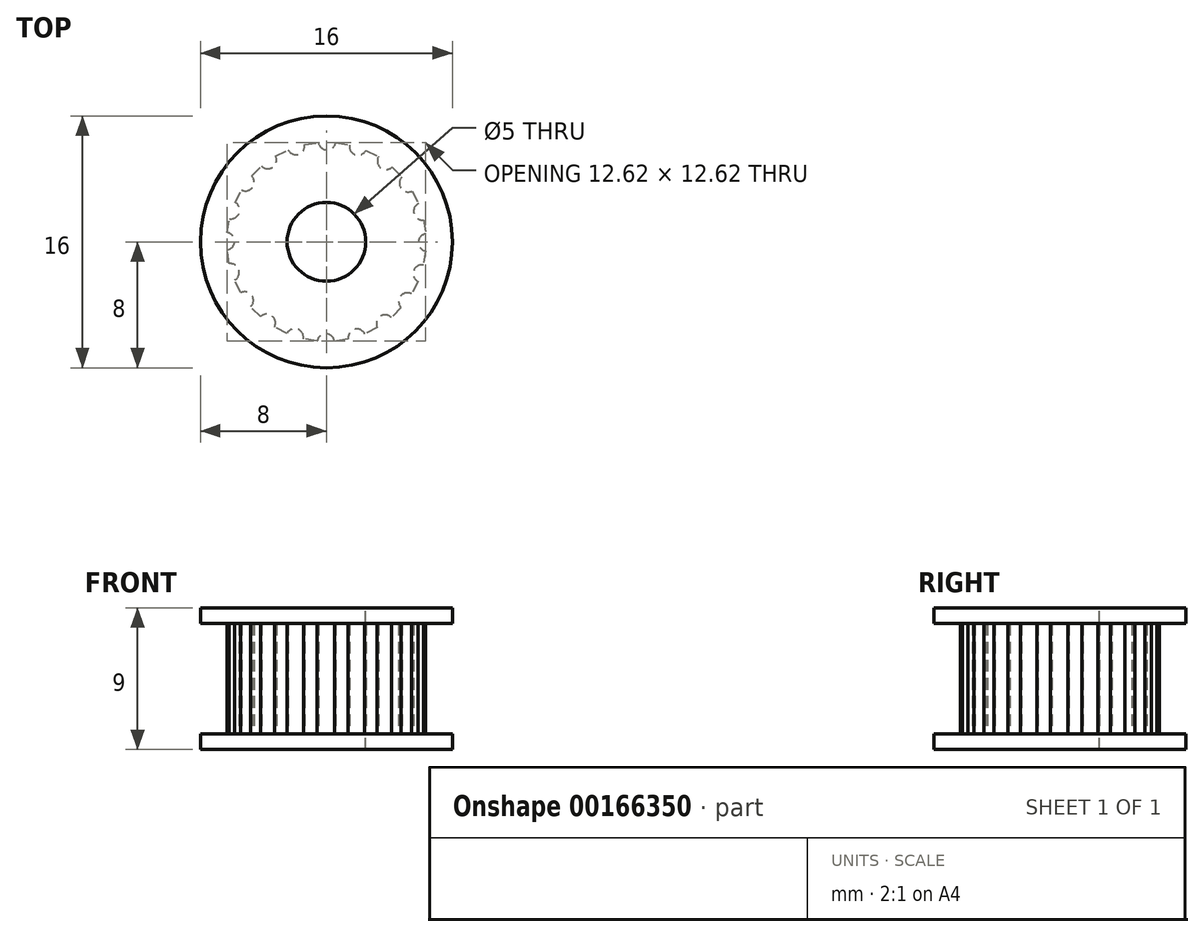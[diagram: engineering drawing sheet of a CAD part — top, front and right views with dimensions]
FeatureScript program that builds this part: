
annotation { "Feature Type Name" : "Feature", "Feature Type Description" : "" }
export const myFeature = defineFeature(function(context is Context, id is Id, definition is map)
    precondition{}
    {
        {
            var Q0;
            Q0=qCreatedBy(makeId("Top.planeOp"),FACE);
            var sketch = newSketch(context, id + "F0", { "sketchPlane" : qUnion([Q0])});
            skCircle(sketch, "E0", {"center": v(0, 0) * mm, "radius": 8 * mm});
            skSolve(sketch);
        }
        {
            var Q0;
            Q0 = qSketchRegion(id + "F0", true);
            extrude(context, id + "F1", {"entities" : qUnion([Q0]), "depth" : 1 * mm});
        }
        {
            var Q0;
            Q0=makeQuery(id+"F1.opExtrude","CAP_FACE",FACE,{"disambiguationData":[OSD([sQuery(id+"F0.wireOp",EDGE,"E0")])],"isStart":false});
            var sketch = newSketch(context, id + "F2", { "sketchPlane" : qUnion([Q0])});
            skCircle(sketch, "E1.cCircle", {"center": v(0, 0) * mm, "radius": 6.4 * mm, "construction": true});
            skLineSegment(sketch, "E1.0", {"start": v(2.01, 6.07) * mm, "end": v(3.79, 5.15) * mm});
            skLineSegment(sketch, "E1.1", {"start": v(3.79, 5.15) * mm, "end": v(5.2, 3.72) * mm});
            skLineSegment(sketch, "E1.2", {"start": v(5.2, 3.72) * mm, "end": v(6.1, 1.94) * mm});
            skLineSegment(sketch, "E1.3", {"start": v(6.1, 1.94) * mm, "end": v(6.4, -0.04) * mm});
            skLineSegment(sketch, "E1.4", {"start": v(6.4, -0.04) * mm, "end": v(6.07, -2.01) * mm});
            skLineSegment(sketch, "E1.5", {"start": v(6.07, -2.01) * mm, "end": v(5.15, -3.79) * mm});
            skLineSegment(sketch, "E1.6", {"start": v(5.15, -3.79) * mm, "end": v(3.72, -5.2) * mm});
            skLineSegment(sketch, "E1.7", {"start": v(3.72, -5.2) * mm, "end": v(1.94, -6.1) * mm});
            skLineSegment(sketch, "E1.8", {"start": v(1.94, -6.1) * mm, "end": v(-0.04, -6.4) * mm});
            skLineSegment(sketch, "E1.9", {"start": v(-0.04, -6.4) * mm, "end": v(-2.01, -6.07) * mm});
            skLineSegment(sketch, "E1.10", {"start": v(-2.01, -6.07) * mm, "end": v(-3.79, -5.15) * mm});
            skLineSegment(sketch, "E1.11", {"start": v(-3.79, -5.15) * mm, "end": v(-5.2, -3.72) * mm});
            skLineSegment(sketch, "E1.12", {"start": v(-5.2, -3.72) * mm, "end": v(-6.1, -1.94) * mm});
            skLineSegment(sketch, "E1.13", {"start": v(-6.1, -1.94) * mm, "end": v(-6.4, 0.04) * mm});
            skLineSegment(sketch, "E1.14", {"start": v(-6.4, 0.04) * mm, "end": v(-6.07, 2.01) * mm});
            skLineSegment(sketch, "E1.15", {"start": v(-6.07, 2.01) * mm, "end": v(-5.15, 3.79) * mm});
            skLineSegment(sketch, "E1.16", {"start": v(-5.15, 3.79) * mm, "end": v(-3.72, 5.2) * mm});
            skLineSegment(sketch, "E1.17", {"start": v(-3.72, 5.2) * mm, "end": v(-1.94, 6.1) * mm});
            skLineSegment(sketch, "E1.18", {"start": v(-1.94, 6.1) * mm, "end": v(0.04, 6.4) * mm});
            skLineSegment(sketch, "E1.19", {"start": v(0.04, 6.4) * mm, "end": v(2.01, 6.07) * mm});
            skCircle(sketch, "E2", {"center": v(3.72, -5.2) * mm, "radius": 0.56 * mm});
            skCircle(sketch, "E3.1.0", {"center": v(5.15, -3.79) * mm, "radius": 0.56 * mm});
            skCircle(sketch, "E3.2.0", {"center": v(6.07, -2.01) * mm, "radius": 0.56 * mm});
            skCircle(sketch, "E3.3.0", {"center": v(6.4, -0.04) * mm, "radius": 0.56 * mm});
            skCircle(sketch, "E3.4.0", {"center": v(6.1, 1.94) * mm, "radius": 0.56 * mm});
            skCircle(sketch, "E3.5.0", {"center": v(5.2, 3.72) * mm, "radius": 0.56 * mm});
            skCircle(sketch, "E3.6.0", {"center": v(3.79, 5.15) * mm, "radius": 0.56 * mm});
            skCircle(sketch, "E3.7.0", {"center": v(2.01, 6.07) * mm, "radius": 0.55 * mm});
            skCircle(sketch, "E3.8.0", {"center": v(0.04, 6.4) * mm, "radius": 0.56 * mm});
            skCircle(sketch, "E3.9.0", {"center": v(-1.94, 6.1) * mm, "radius": 0.56 * mm});
            skCircle(sketch, "E3.10.0", {"center": v(-3.72, 5.2) * mm, "radius": 0.56 * mm});
            skCircle(sketch, "E3.11.0", {"center": v(-5.15, 3.79) * mm, "radius": 0.56 * mm});
            skCircle(sketch, "E3.12.0", {"center": v(-6.07, 2.01) * mm, "radius": 0.56 * mm});
            skCircle(sketch, "E3.13.0", {"center": v(-6.4, 0.04) * mm, "radius": 0.56 * mm});
            skCircle(sketch, "E3.14.0", {"center": v(-6.1, -1.94) * mm, "radius": 0.56 * mm});
            skCircle(sketch, "E3.15.0", {"center": v(-5.2, -3.72) * mm, "radius": 0.56 * mm});
            skCircle(sketch, "E3.16.0", {"center": v(-3.79, -5.15) * mm, "radius": 0.56 * mm});
            skCircle(sketch, "E3.17.0", {"center": v(-2.01, -6.07) * mm, "radius": 0.56 * mm});
            skCircle(sketch, "E3.18.0", {"center": v(-0.04, -6.4) * mm, "radius": 0.56 * mm});
            skCircle(sketch, "E3.19.0", {"center": v(1.94, -6.1) * mm, "radius": 0.56 * mm});
            skSolve(sketch);
        }
        {
            var Q0;
            {var subQ67=sQuery(id+"F2.wireOp",EDGE,"E3.7.0");var subQ77=sQuery(id+"F2.wireOp",EDGE,"E1.0");var subQ78=makeQuery(id+"F2.imprint","INTERSECT",VERTEX,{"derivedFrom":[subQ77,subQ67]});Q0=makeQuery(id+"F2.imprint","IMPRINT",FACE,{"disambiguationData":[TD([[makeQuery(id+"F2.imprint","IMPRINT",EDGE,{"disambiguationData":[TD([[subQ78,-1.0]])],"derivedFrom":subQ77}),-1.0]])]});}
            extrude(context, id + "F3", {"entities" : qUnion([Q0]), "operationType" : NewBodyOperationType.ADD, "depth" : 7 * mm});
        }
        {
            var Q0;
            Q0=makeQuery(id+"F3.opExtrude","CAP_FACE",FACE,{"disambiguationData":[OSD([sQuery(id+"F2.wireOp",EDGE,"E1.0"),sQuery(id+"F2.wireOp",EDGE,"E1.1"),sQuery(id+"F2.wireOp",EDGE,"E1.2"),sQuery(id+"F2.wireOp",EDGE,"E1.3"),sQuery(id+"F2.wireOp",EDGE,"E1.4"),sQuery(id+"F2.wireOp",EDGE,"E1.5"),sQuery(id+"F2.wireOp",EDGE,"E1.6"),sQuery(id+"F2.wireOp",EDGE,"E1.7"),sQuery(id+"F2.wireOp",EDGE,"E1.8"),sQuery(id+"F2.wireOp",EDGE,"E1.9"),sQuery(id+"F2.wireOp",EDGE,"E1.10"),sQuery(id+"F2.wireOp",EDGE,"E1.11"),sQuery(id+"F2.wireOp",EDGE,"E1.12"),sQuery(id+"F2.wireOp",EDGE,"E1.13"),sQuery(id+"F2.wireOp",EDGE,"E1.14"),sQuery(id+"F2.wireOp",EDGE,"E1.15"),sQuery(id+"F2.wireOp",EDGE,"E1.16"),sQuery(id+"F2.wireOp",EDGE,"E1.17"),sQuery(id+"F2.wireOp",EDGE,"E1.18"),sQuery(id+"F2.wireOp",EDGE,"E1.19"),sQuery(id+"F2.wireOp",EDGE,"E2"),sQuery(id+"F2.wireOp",EDGE,"E3.1.0"),sQuery(id+"F2.wireOp",EDGE,"E3.2.0"),sQuery(id+"F2.wireOp",EDGE,"E3.3.0"),sQuery(id+"F2.wireOp",EDGE,"E3.4.0"),sQuery(id+"F2.wireOp",EDGE,"E3.5.0"),sQuery(id+"F2.wireOp",EDGE,"E3.6.0"),sQuery(id+"F2.wireOp",EDGE,"E3.7.0"),sQuery(id+"F2.wireOp",EDGE,"E3.8.0"),sQuery(id+"F2.wireOp",EDGE,"E3.9.0"),sQuery(id+"F2.wireOp",EDGE,"E3.10.0"),sQuery(id+"F2.wireOp",EDGE,"E3.11.0"),sQuery(id+"F2.wireOp",EDGE,"E3.12.0"),sQuery(id+"F2.wireOp",EDGE,"E3.13.0"),sQuery(id+"F2.wireOp",EDGE,"E3.14.0"),sQuery(id+"F2.wireOp",EDGE,"E3.15.0"),sQuery(id+"F2.wireOp",EDGE,"E3.16.0"),sQuery(id+"F2.wireOp",EDGE,"E3.17.0"),sQuery(id+"F2.wireOp",EDGE,"E3.18.0"),sQuery(id+"F2.wireOp",EDGE,"E3.19.0")])],"isStart":false});
            var sketch = newSketch(context, id + "F4", { "sketchPlane" : qUnion([Q0])});
            skCircle(sketch, "E4", {"center": v(0, 0) * mm, "radius": 8 * mm});
            skSolve(sketch);
        }
        {
            var Q0;
            Q0 = qSketchRegion(id + "F4", true);
            extrude(context, id + "F5", {"entities" : qUnion([Q0]), "operationType" : NewBodyOperationType.ADD, "depth" : 1 * mm});
        }
        {
            var Q0;
            Q0=makeQuery(id+"F5.opExtrude","CAP_FACE",FACE,{"disambiguationData":[OSD([sQuery(id+"F4.wireOp",EDGE,"E4")])],"isStart":false});
            var sketch = newSketch(context, id + "F6", { "sketchPlane" : qUnion([Q0])});
            skCircle(sketch, "E5", {"center": v(0, 0) * mm, "radius": 2.5 * mm});
            skSolve(sketch);
        }
        {
            var Q0;
            Q0 = qSketchRegion(id + "F6", true);
            extrude(context, id + "F7", {"entities" : qUnion([Q0]), "operationType" : NewBodyOperationType.REMOVE, "oppositeDirection" : true, "depth" : 9 * mm});
        }
    });
